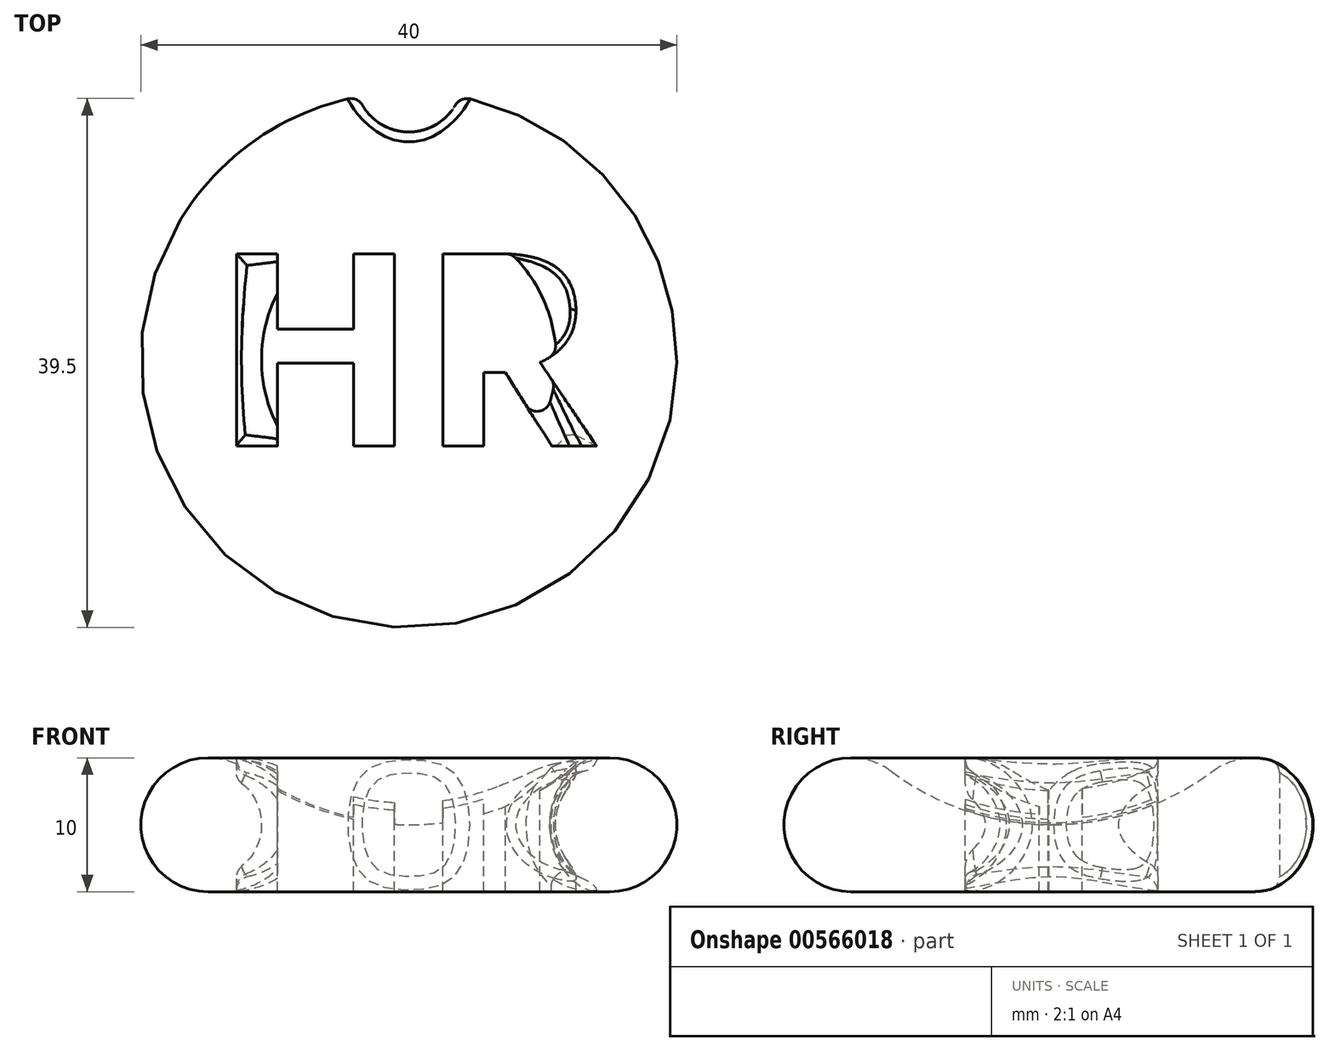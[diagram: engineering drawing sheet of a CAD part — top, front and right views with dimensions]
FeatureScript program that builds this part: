
annotation { "Feature Type Name" : "Feature", "Feature Type Description" : "" }
export const myFeature = defineFeature(function(context is Context, id is Id, definition is map)
    precondition{}
    {
        {
            var Q0;
            Q0=qCreatedBy(makeId("Front.planeOp"),FACE);
            var sketch = newSketch(context, id + "F0", { "sketchPlane" : qUnion([Q0])});
            skArc(sketch, "E0", {"start": v(-12, 9) * mm, "mid": v(-19.74, 6.58) * mm, "end": v(-15, 0) * mm});
            skArc(sketch, "E1", {"start": v(-12, 9) * mm, "mid": v(-6.32, 6.03) * mm, "end": v(0, 5) * mm});
            skLineSegment(sketch, "E2", {"start": v(0, 0) * mm, "end": v(-15, 0) * mm});
            skLineSegment(sketch, "E3", {"start": v(0, 0) * mm, "end": v(0, 5) * mm});
            skSolve(sketch);
        }
        {
            var Q0;
            Q0=makeQuery(id+"F0.imprint","IMPRINT",FACE,{"disambiguationData":[TD([[makeQuery(id+"F0.imprint","IMPRINT",EDGE,{"derivedFrom":sQuery(id+"F0.wireOp",EDGE,"E0")}),1.0]])]});
            var Q1;
            Q1=sQuery(id+"F0.wireOp",EDGE,"E3");
            revolve(context, id + "F1", {"entities" : qUnion([Q0]), "axis" : qUnion([Q1]), "revolveType" : RevolveType.FULL});
        }
        {
            var Q0;
            Q0=qCreatedBy(makeId("Top.planeOp"),FACE);
            cPlane(context, id + "F2", {"entities" : qUnion([Q0]), "cplaneType" : CPlaneType.OFFSET, "offset" : 10 * mm, "width" : 150 * mm, "height" : 150 * mm});
        }
        {
            var Q0;
            Q0=qCreatedBy(id+"F2.planeOp",FACE);
            var sketch = newSketch(context, id + "F3", { "sketchPlane" : qUnion([Q0])});
            skText(sketch, "E4", { "text": "HR", "fontName": "OpenSans-Bold.ttf"});
            const initialGuessF3  = {"E4": [-0.01468, -0.00647, 1, 0, 0.0145]};
            skSetInitialGuess(sketch, initialGuessF3);
            skSolve(sketch);
        }
        {
            var Q0;
            Q0=qSketchRegion(id+"F3",true);
            extrude(context, id + "F4", {"entities" : qUnion([Q0]), "operationType" : NewBodyOperationType.REMOVE, "oppositeDirection" : true, "depth" : 25 * mm});
        }
        {
            var Q0;
            Q0=makeQuery(id+"F3.imprint","IMPRINT",FACE,{"disambiguationData":[TD([[makeQuery(id+"F3.imprint","IMPRINT",EDGE,{"derivedFrom":sQuery(id+"F3.wireOp",EDGE,"E4.sketch_text.stroke-12")}),1.0]])]});
            extrude(context, id + "F5", {"entities" : qUnion([Q0]), "operationType" : NewBodyOperationType.REMOVE, "oppositeDirection" : true, "depth" : 25 * mm});
        }
        {
            var Q0;
            Q0=qCreatedBy(makeId("Front.planeOp"),FACE);
            var sketch = newSketch(context, id + "F6", { "sketchPlane" : qUnion([Q0])});
            skCircle(sketch, "E5.0", {"center": v(-15, 5) * mm, "radius": 4 * mm});
            skSolve(sketch);
        }
        {
            var Q0;
            Q0=makeQuery(id+"F6.imprint","IMPRINT",FACE,{"disambiguationData":[TD([[makeQuery(id+"F6.imprint","IMPRINT",EDGE,{"derivedFrom":sQuery(id+"F6.wireOp",EDGE,"E5.0")}),1.0]])]});
            var Q1;
            Q1=sQuery(id+"F0.wireOp",EDGE,"E3");
            revolve(context, id + "F7", {"operationType" : NewBodyOperationType.ADD, "entities" : qUnion([Q0]), "axis" : qUnion([Q1]), "revolveType" : RevolveType.FULL});
        }
        {
            var Q0;
            Q0=qCreatedBy(makeId("Top.planeOp"),FACE);
            var sketch = newSketch(context, id + "F8", { "sketchPlane" : qUnion([Q0])});
            skCircle(sketch, "E6", {"center": v(0, 21) * mm, "radius": 4 * mm});
            skSolve(sketch);
        }
        {
            var Q0;
            Q0=makeQuery(id+"F8.imprint","IMPRINT",FACE,{"disambiguationData":[TD([[makeQuery(id+"F8.imprint","IMPRINT",EDGE,{"derivedFrom":sQuery(id+"F8.wireOp",EDGE,"E6")}),1.0]])]});
            extrude(context, id + "F9", {"entities" : qUnion([Q0]), "operationType" : NewBodyOperationType.REMOVE, "depth" : 23.3 * mm});
        }
        {
            var Q0;
            Q0=makeQuery(id+"F9.boolean.opBoolean","INTERSECT",EDGE,{"derivedFrom":[makeQuery(id+"F4.boolean.opBoolean","SPLIT",FACE,{"disambiguationData":[TD([makeQuery(id+"F1.opRevolve","SWEPT_FACE",FACE,{"disambiguationData":[OSD([sQuery(id+"F0.wireOp",EDGE,"E2")])]})])],"derivedFrom":makeQuery(id+"F1.opRevolve","SWEPT_FACE",FACE,{"disambiguationData":[OSD([sQuery(id+"F0.wireOp",EDGE,"E0")])]})}),makeQuery(id+"F9.opExtrude","SWEPT_FACE",FACE,{"disambiguationData":[OSD([sQuery(id+"F8.wireOp",EDGE,"E6")])]})]});
            fillet(context, id + "F10", {"entities" : qUnion([Q0]), "radius" : 1 * mm, "tangentPropagation" : true, "allowEdgeOverflow" : false});
        }
        {
            var Q0;
            Q0=makeQuery(id+"F7.boolean.opBoolean","INTERSECT",EDGE,{"disambiguationData":[OD(0.0)],"derivedFrom":[makeQuery(id+"F4.boolean.opBoolean","COPY",FACE,{"derivedFrom":makeQuery(id+"F4.opExtrude","SWEPT_FACE",FACE,{"disambiguationData":[OSD([sQuery(id+"F3.wireOp",EDGE,"E4.sketch_text.stroke-5")])]})}),makeQuery(id+"F7.opRevolve","SWEPT_FACE",FACE,{"disambiguationData":[OSD([sQuery(id+"F6.wireOp",EDGE,"E5.0")])]})]});
            var Q1;
            Q1=makeQuery(id+"F7.boolean.opBoolean","INTERSECT",EDGE,{"disambiguationData":[OD(0.0)],"derivedFrom":[makeQuery(id+"F4.boolean.opBoolean","COPY",FACE,{"derivedFrom":makeQuery(id+"F4.opExtrude","SWEPT_FACE",FACE,{"disambiguationData":[OSD([sQuery(id+"F3.wireOp",EDGE,"E4.sketch_text.stroke-6")])]})}),makeQuery(id+"F7.opRevolve","SWEPT_FACE",FACE,{"disambiguationData":[OSD([sQuery(id+"F6.wireOp",EDGE,"E5.0")])]})]});
            var Q2;
            Q2=makeQuery(id+"F7.boolean.opBoolean","INTERSECT",EDGE,{"disambiguationData":[OD(1.0)],"derivedFrom":[makeQuery(id+"F4.boolean.opBoolean","COPY",FACE,{"derivedFrom":makeQuery(id+"F4.opExtrude","SWEPT_FACE",FACE,{"disambiguationData":[OSD([sQuery(id+"F3.wireOp",EDGE,"E4.sketch_text.stroke-4")])]})}),makeQuery(id+"F7.opRevolve","SWEPT_FACE",FACE,{"disambiguationData":[OSD([sQuery(id+"F6.wireOp",EDGE,"E5.0")])]})]});
            fillet(context, id + "F11", {"entities" : qUnion([Q0, Q1, Q2]), "radius" : 1 * mm, "tangentPropagation" : true, "allowEdgeOverflow" : false});
        }
        {
            var Q0;
            Q0=makeQuery(id+"F7.boolean.opBoolean","INTERSECT",EDGE,{"disambiguationData":[OD(0.0)],"derivedFrom":[makeQuery(id+"F4.boolean.opBoolean","COPY",FACE,{"derivedFrom":makeQuery(id+"F4.opExtrude","SWEPT_FACE",FACE,{"disambiguationData":[OSD([sQuery(id+"F3.wireOp",EDGE,"E4.sketch_text.stroke-28")])]})}),makeQuery(id+"F7.opRevolve","SWEPT_FACE",FACE,{"disambiguationData":[OSD([sQuery(id+"F6.wireOp",EDGE,"E5.0")])]})]});
            var Q1;
            Q1=makeQuery(id+"F7.boolean.opBoolean","INTERSECT",EDGE,{"derivedFrom":[makeQuery(id+"F4.boolean.opBoolean","COPY",FACE,{"derivedFrom":makeQuery(id+"F4.opExtrude","SWEPT_FACE",FACE,{"disambiguationData":[OSD([sQuery(id+"F3.wireOp",EDGE,"E4.sketch_text.stroke-29")])]})}),makeQuery(id+"F7.opRevolve","SWEPT_FACE",FACE,{"disambiguationData":[OSD([sQuery(id+"F6.wireOp",EDGE,"E5.0")])]})]});
            var Q2;
            Q2=makeQuery(id+"F7.boolean.opBoolean","INTERSECT",EDGE,{"derivedFrom":[makeQuery(id+"F4.boolean.opBoolean","COPY",FACE,{"derivedFrom":makeQuery(id+"F4.opExtrude","SWEPT_FACE",FACE,{"disambiguationData":[OSD([sQuery(id+"F3.wireOp",EDGE,"E4.sketch_text.stroke-27")])]})}),makeQuery(id+"F7.opRevolve","SWEPT_FACE",FACE,{"disambiguationData":[OSD([sQuery(id+"F6.wireOp",EDGE,"E5.0")])]})]});
            var Q3;
            Q3=makeQuery(id+"F7.boolean.opBoolean","INTERSECT",EDGE,{"disambiguationData":[OD(1.0)],"derivedFrom":[makeQuery(id+"F4.boolean.opBoolean","COPY",FACE,{"derivedFrom":makeQuery(id+"F4.opExtrude","SWEPT_FACE",FACE,{"disambiguationData":[OSD([sQuery(id+"F3.wireOp",EDGE,"E4.sketch_text.stroke-25")])]})}),makeQuery(id+"F7.opRevolve","SWEPT_FACE",FACE,{"disambiguationData":[OSD([sQuery(id+"F6.wireOp",EDGE,"E5.0")])]})]});
            var Q4;
            Q4=makeQuery(id+"F7.boolean.opBoolean","INTERSECT",EDGE,{"derivedFrom":[makeQuery(id+"F4.boolean.opBoolean","COPY",FACE,{"derivedFrom":makeQuery(id+"F4.opExtrude","SWEPT_FACE",FACE,{"disambiguationData":[OSD([sQuery(id+"F3.wireOp",EDGE,"E4.sketch_text.stroke-26")])]})}),makeQuery(id+"F7.opRevolve","SWEPT_FACE",FACE,{"disambiguationData":[OSD([sQuery(id+"F6.wireOp",EDGE,"E5.0")])]})]});
            var Q5;
            Q5=makeQuery(id+"F7.boolean.opBoolean","INTERSECT",EDGE,{"disambiguationData":[OD(1.0)],"derivedFrom":[makeQuery(id+"F4.boolean.opBoolean","COPY",FACE,{"derivedFrom":makeQuery(id+"F4.opExtrude","SWEPT_FACE",FACE,{"disambiguationData":[OSD([sQuery(id+"F3.wireOp",EDGE,"E4.sketch_text.stroke-24")])]})}),makeQuery(id+"F7.opRevolve","SWEPT_FACE",FACE,{"disambiguationData":[OSD([sQuery(id+"F6.wireOp",EDGE,"E5.0")])]})]});
            var Q6;
            Q6=makeQuery(id+"F7.boolean.opBoolean","INTERSECT",EDGE,{"derivedFrom":[makeQuery(id+"F4.boolean.opBoolean","COPY",FACE,{"derivedFrom":makeQuery(id+"F4.opExtrude","SWEPT_FACE",FACE,{"disambiguationData":[OSD([sQuery(id+"F3.wireOp",EDGE,"E4.sketch_text.stroke-23")])]})}),makeQuery(id+"F7.opRevolve","SWEPT_FACE",FACE,{"disambiguationData":[OSD([sQuery(id+"F6.wireOp",EDGE,"E5.0")])]})]});
            fillet(context, id + "F12", {"entities" : qUnion([Q0, Q1, Q2, Q3, Q4, Q5, Q6]), "radius" : 1 * mm, "tangentPropagation" : true, "allowEdgeOverflow" : false});
        }
        {
            var Q0;
            Q0=makeQuery(id+"F7.boolean.opBoolean","INTERSECT",EDGE,{"disambiguationData":[OD(0.0)],"derivedFrom":[makeQuery(id+"F4.boolean.opBoolean","COPY",FACE,{"derivedFrom":makeQuery(id+"F4.opExtrude","SWEPT_FACE",FACE,{"disambiguationData":[OSD([sQuery(id+"F3.wireOp",EDGE,"E4.sketch_text.stroke-4")])]})}),makeQuery(id+"F7.opRevolve","SWEPT_FACE",FACE,{"disambiguationData":[OSD([sQuery(id+"F6.wireOp",EDGE,"E5.0")])]})]});
            var Q1;
            Q1=makeQuery(id+"F7.boolean.opBoolean","INTERSECT",EDGE,{"disambiguationData":[OD(1.0)],"derivedFrom":[makeQuery(id+"F4.boolean.opBoolean","COPY",FACE,{"derivedFrom":makeQuery(id+"F4.opExtrude","SWEPT_FACE",FACE,{"disambiguationData":[OSD([sQuery(id+"F3.wireOp",EDGE,"E4.sketch_text.stroke-5")])]})}),makeQuery(id+"F7.opRevolve","SWEPT_FACE",FACE,{"disambiguationData":[OSD([sQuery(id+"F6.wireOp",EDGE,"E5.0")])]})]});
            var Q2;
            Q2=makeQuery(id+"F7.boolean.opBoolean","INTERSECT",EDGE,{"disambiguationData":[OD(1.0)],"derivedFrom":[makeQuery(id+"F4.boolean.opBoolean","COPY",FACE,{"derivedFrom":makeQuery(id+"F4.opExtrude","SWEPT_FACE",FACE,{"disambiguationData":[OSD([sQuery(id+"F3.wireOp",EDGE,"E4.sketch_text.stroke-6")])]})}),makeQuery(id+"F7.opRevolve","SWEPT_FACE",FACE,{"disambiguationData":[OSD([sQuery(id+"F6.wireOp",EDGE,"E5.0")])]})]});
            fillet(context, id + "F13", {"entities" : qUnion([Q0, Q1, Q2]), "radius" : 1 * mm, "tangentPropagation" : true, "allowEdgeOverflow" : false});
        }
    });
